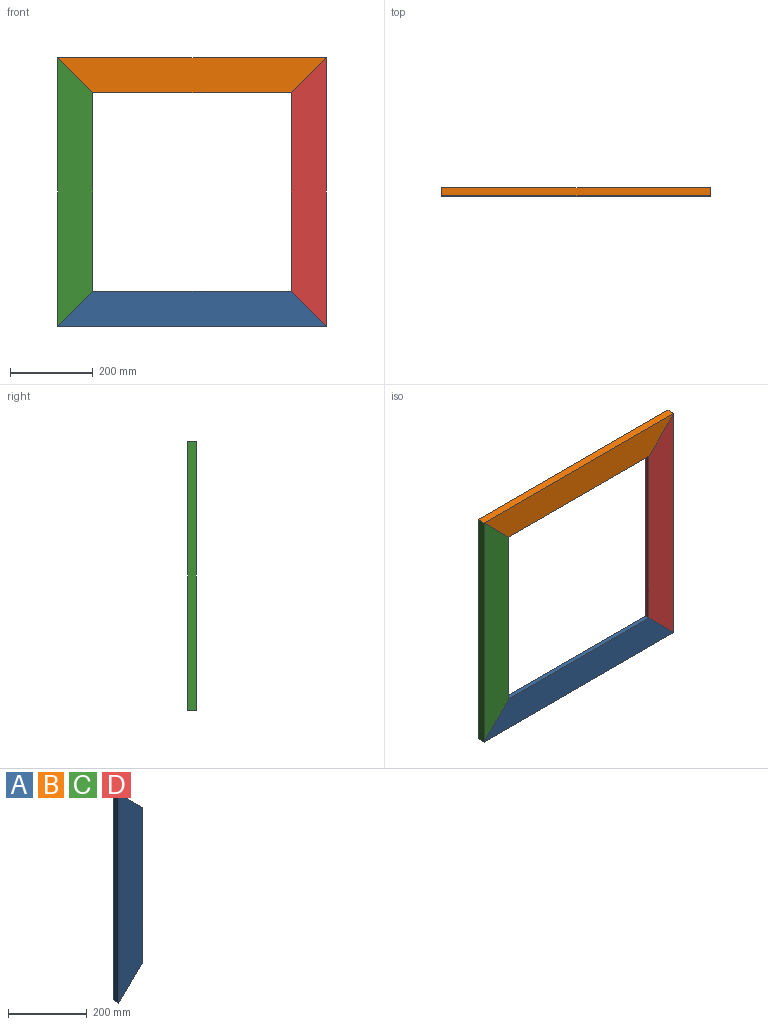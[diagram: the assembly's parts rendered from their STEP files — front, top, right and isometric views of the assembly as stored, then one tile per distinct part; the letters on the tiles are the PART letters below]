
ASSEMBLY  parts=4 mates=6
PART A: 8 faces, bbox 85x20x650 mm
  f0: plane 85x85mm, normal (0.71,0,0.71), area 2139mm2, adj f2,f3,f4,f5,f6,f7
  f1: plane 85x85mm, normal (0.71,0,-0.71), area 2139mm2, adj f2,f3,f4,f5,f6,f7
  f2: plane 650x20mm, normal (-1,0,0), area 13000mm2, adj f0,f1,f4,f5
  f3: plane 480x12.5mm, normal (1,0,0), area 6000mm2, adj f0,f1,f4,f6
  f4: plane 650x85mm, normal (0,-1,0), area 48025mm2, adj f0,f1,f2,f3
  f5: plane 650x60mm, normal (0,1,0), area 35400mm2, adj f0,f1,f2,f7
  f6: plane 530x25mm, normal (0,1,0), area 12625mm2, adj f0,f1,f3,f7
  f7: plane 530x7.5mm, normal (1,0,0), area 3975mm2, adj f0,f1,f5,f6
PART B: same geometry as A
PART C: same geometry as A
PART D: same geometry as A
PLACE A rot(axis=(0,-1,0),90deg) t=(112.44,-188.63,-205.96)mm
PLACE B rot(axis=(0,1,0),90deg) t=(112.44,-188.63,359.04)mm
PLACE C t=(-170.06,-188.63,76.54)mm
PLACE D rot(axis=(0,-1,0),180deg) t=(394.94,-188.63,76.54)mm
MATE planar A.f4 <-> C.f4  axis (0,-1,0) through (112.44,-208.63,-208.09)mm
MATE fastened B.f1 <-> C.f0  axis (-0.71,0,-0.71) through (-173.78,-199.41,362.76)mm
MATE fastened A.f1 <-> D.f0  axis (0.71,0,0.71) through (398.66,-199.41,-209.68)mm
MATE planar D.f4 <-> C.f4  axis (0,-1,0) through (397.07,-208.63,76.54)mm
MATE planar B.f4 <-> C.f4  axis (0,-1,0) through (112.44,-208.63,361.17)mm
MATE fastened A.f0 <-> C.f1  axis (-0.71,0,0.71) through (-173.78,-199.41,-209.68)mm
